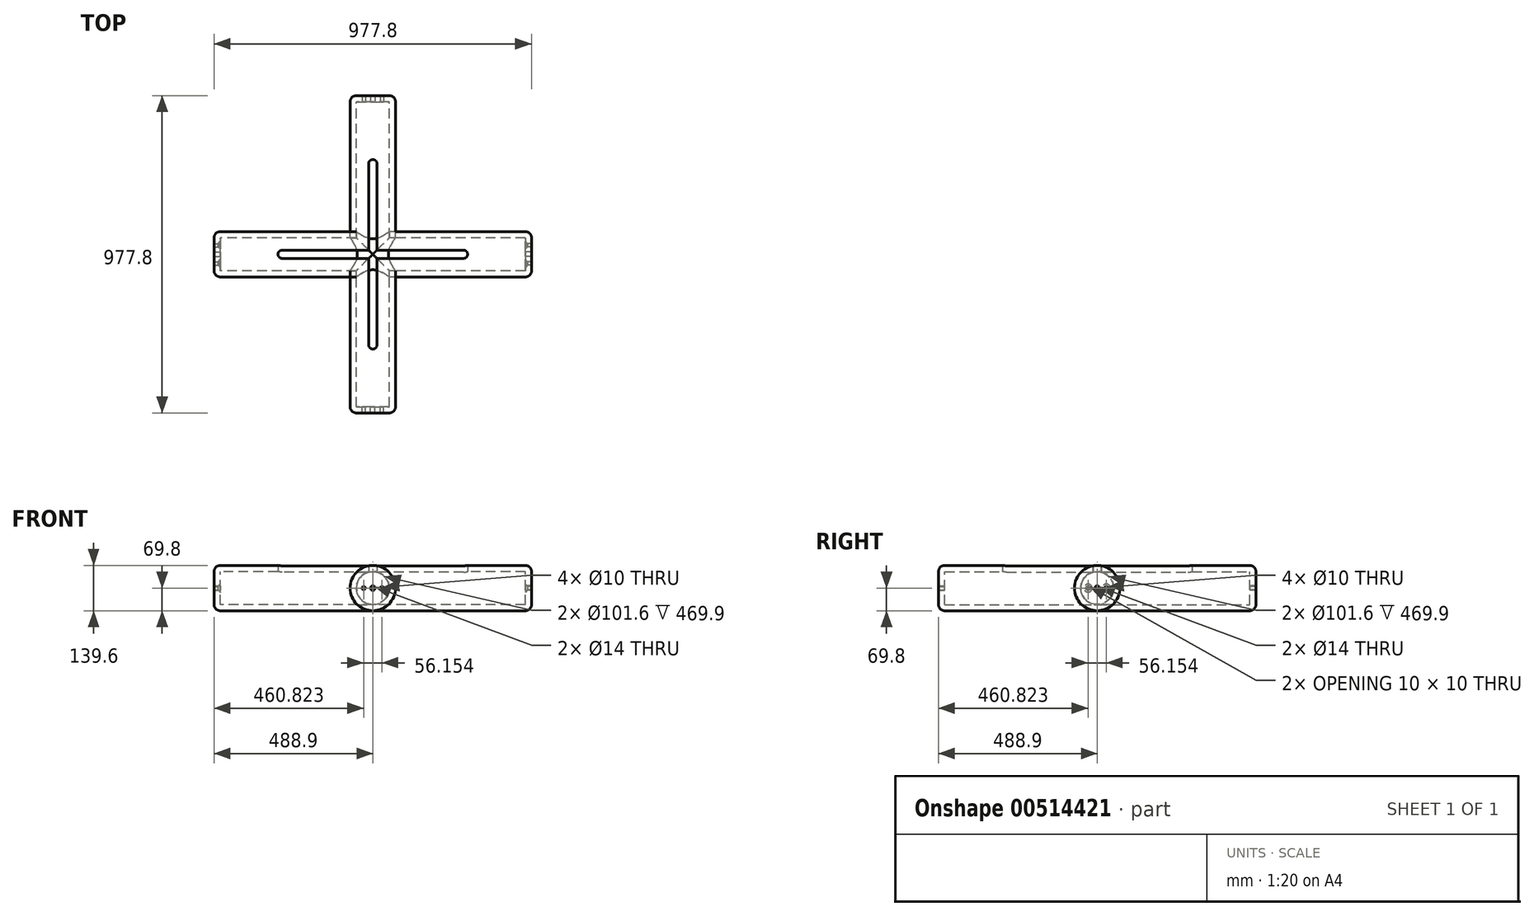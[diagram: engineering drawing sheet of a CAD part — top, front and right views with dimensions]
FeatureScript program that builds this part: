
annotation { "Feature Type Name" : "Feature", "Feature Type Description" : "" }
export const myFeature = defineFeature(function(context is Context, id is Id, definition is map)
    precondition{}
    {
        {
            var Q0;
            Q0=qCreatedBy(makeId("Front.planeOp"),FACE);
            var sketch = newSketch(context, id + "F0", { "sketchPlane" : qUnion([Q0])});
            skLineSegment(sketch, "E0", {"start": v(0, 19.05) * mm, "end": v(0, -19.05) * mm, "construction": true});
            skLineSegment(sketch, "E1", {"start": v(-19.05, 0) * mm, "end": v(19.05, 0) * mm, "construction": true});
            skPoint(sketch, "E2", {"position": v(0, 0) * mm});
            skCircle(sketch, "E3", {"center": v(0, 0) * mm, "radius": 50.8 * mm});
            skCircle(sketch, "E4.0", {"center": v(0, 0) * mm, "radius": 69.8 * mm});
            skSolve(sketch);
        }
        {
            var Q0;
            Q0=makeQuery(id+"F0.imprint","IMPRINT",FACE,{"disambiguationData":[TD([[makeQuery(id+"F0.imprint","IMPRINT",EDGE,{"derivedFrom":sQuery(id+"F0.wireOp",EDGE,"E3")}),-1.0]])]});
            extrude(context, id + "F1", {"entities" : qUnion([Q0]), "depth" : 939.8 * mm, "offsetDistance" : 25.4 * mm, "symmetric" : true});
        }
        {
            var Q0;
            Q0=qCreatedBy(makeId("Right.planeOp"),FACE);
            var sketch = newSketch(context, id + "F2", { "sketchPlane" : qUnion([Q0])});
            skPoint(sketch, "E5", {"position": v(0, 0) * mm});
            skCircle(sketch, "E6", {"center": v(0, 0) * mm, "radius": 50.8 * mm});
            skCircle(sketch, "E7.0", {"center": v(0, 0) * mm, "radius": 69.8 * mm});
            skSolve(sketch);
        }
        {
            var Q0;
            Q0=makeQuery(id+"F2.imprint","IMPRINT",FACE,{"disambiguationData":[TD([[makeQuery(id+"F2.imprint","IMPRINT",EDGE,{"derivedFrom":sQuery(id+"F2.wireOp",EDGE,"E6")}),-1.0]])]});
            extrude(context, id + "F3", {"entities" : qUnion([Q0]), "depth" : 939.8 * mm, "offsetDistance" : 25.4 * mm, "symmetric" : true});
        }
        {
            var Q0;
            Q0=sQuery(id+"F2.wireOp",VERTEX,"E5");
            var Q1;
            Q1=makeQuery(id+"F1.opExtrude","SWEPT_BODY",BODY,{"disambiguationData":[OSD([sQuery(id+"F0.wireOp",EDGE,"E3"),sQuery(id+"F0.wireOp",EDGE,"E4.0")])]});
            hole(context, id + "F4", {"style" : HoleStyle.SIMPLE, "endStyle" : HoleEndStyle.THROUGH, "oppositeDirection" : true, "holeDiameter" : 101.6 * mm, "isTappedThrough" : true, "tappedDepth" : 12.7 * mm, "tapClearance" : 3, "locations" : qUnion([Q0]), "scope" : qUnion([Q1]), "majorDiameter" : 6.35 * mm});
        }
        {
            var Q0;
            Q0=sQuery(id+"F2.wireOp",VERTEX,"E5");
            var Q1;
            Q1=makeQuery(id+"F1.opExtrude","SWEPT_BODY",BODY,{"disambiguationData":[OSD([sQuery(id+"F0.wireOp",EDGE,"E3"),sQuery(id+"F0.wireOp",EDGE,"E4.0")])]});
            hole(context, id + "F5", {"style" : HoleStyle.SIMPLE, "endStyle" : HoleEndStyle.THROUGH, "holeDiameter" : 101.6 * mm, "isTappedThrough" : true, "tappedDepth" : 12.7 * mm, "tapClearance" : 3, "locations" : qUnion([Q0]), "scope" : qUnion([Q1]), "majorDiameter" : 6.35 * mm});
        }
        {
            var Q0;
            Q0=sQuery(id+"F0.wireOp",VERTEX,"E2");
            var Q1;
            Q1=makeQuery(id+"F3.opExtrude","SWEPT_BODY",BODY,{"disambiguationData":[OSD([sQuery(id+"F2.wireOp",EDGE,"E6"),sQuery(id+"F2.wireOp",EDGE,"E7.0")])]});
            hole(context, id + "F6", {"style" : HoleStyle.SIMPLE, "endStyle" : HoleEndStyle.THROUGH, "oppositeDirection" : true, "holeDiameter" : 101.6 * mm, "isTappedThrough" : true, "tappedDepth" : 12.7 * mm, "tapClearance" : 3, "locations" : qUnion([Q0]), "scope" : qUnion([Q1]), "majorDiameter" : 6.35 * mm});
        }
        {
            var Q0;
            Q0=sQuery(id+"F0.wireOp",VERTEX,"E2");
            var Q1;
            Q1=makeQuery(id+"F3.opExtrude","SWEPT_BODY",BODY,{"disambiguationData":[OSD([sQuery(id+"F2.wireOp",EDGE,"E6"),sQuery(id+"F2.wireOp",EDGE,"E7.0")])]});
            hole(context, id + "F7", {"style" : HoleStyle.SIMPLE, "endStyle" : HoleEndStyle.THROUGH, "holeDiameter" : 101.6 * mm, "isTappedThrough" : true, "tappedDepth" : 12.7 * mm, "tapClearance" : 3, "locations" : qUnion([Q0]), "scope" : qUnion([Q1]), "majorDiameter" : 6.35 * mm});
        }
        {
            var Q0;
            Q0=qCreatedBy(makeId("Top.planeOp"),FACE);
            var sketch = newSketch(context, id + "F8", { "sketchPlane" : qUnion([Q0])});
            skLineSegment(sketch, "E8.bottom", {"start": v(-12.7, 419.1) * mm, "end": v(12.7, 419.1) * mm});
            skLineSegment(sketch, "E8.top", {"start": v(-12.7, -419.1) * mm, "end": v(12.7, -419.1) * mm});
            skLineSegment(sketch, "E8.left", {"start": v(-12.7, 419.1) * mm, "end": v(-12.7, -419.1) * mm});
            skLineSegment(sketch, "E8.right", {"start": v(12.7, 419.1) * mm, "end": v(12.7, -419.1) * mm});
            skLineSegment(sketch, "E9.bottom", {"start": v(-419.1, 12.7) * mm, "end": v(419.1, 12.7) * mm});
            skLineSegment(sketch, "E9.top", {"start": v(-419.1, -12.7) * mm, "end": v(419.1, -12.7) * mm});
            skLineSegment(sketch, "E9.left", {"start": v(-419.1, 12.7) * mm, "end": v(-419.1, -12.7) * mm});
            skLineSegment(sketch, "E9.right", {"start": v(419.1, 12.7) * mm, "end": v(419.1, -12.7) * mm});
            skArc(sketch, "E10", {"start": v(12.7, 279.4) * mm, "mid": v(0, 292.1) * mm, "end": v(-12.7, 279.4) * mm});
            skLineSegment(sketch, "E11", {"start": v(0, 279.4) * mm, "end": v(0, 0) * mm, "construction": true});
            skArc(sketch, "E12.1.0", {"start": v(-279.4, 12.7) * mm, "mid": v(-292.1, 0) * mm, "end": v(-279.4, -12.7) * mm});
            skArc(sketch, "E12.2.0", {"start": v(-12.7, -279.4) * mm, "mid": v(0, -292.1) * mm, "end": v(12.7, -279.4) * mm});
            skArc(sketch, "E12.3.0", {"start": v(279.4, -12.7) * mm, "mid": v(292.1, 0) * mm, "end": v(279.4, 12.7) * mm});
            skPoint(sketch, "E12.center", {"position": v(0, 0) * mm});
            skCircle(sketch, "E13", {"center": v(0, 0) * mm, "radius": 12.7 * mm, "construction": true});
            skSolve(sketch);
        }
        {
            var Q0;
            {var subQ5=sQuery(id+"F8.wireOp",EDGE,"E12.1.0");Q0=makeQuery(id+"F8.imprint","IMPRINT",FACE,{"disambiguationData":[TD([[makeQuery(id+"F8.imprint","IMPRINT",EDGE,{"derivedFrom":subQ5}),1.0]])]});}
            var Q1;
            {var subQ0=sQuery(id+"F8.wireOp",EDGE,"E10");Q1=makeQuery(id+"F8.imprint","IMPRINT",FACE,{"disambiguationData":[TD([[makeQuery(id+"F8.imprint","IMPRINT",EDGE,{"derivedFrom":subQ0}),1.0]])]});}
            var Q2;
            {var subQ5=sQuery(id+"F8.wireOp",EDGE,"E12.3.0");Q2=makeQuery(id+"F8.imprint","IMPRINT",FACE,{"disambiguationData":[TD([[makeQuery(id+"F8.imprint","IMPRINT",EDGE,{"derivedFrom":subQ5}),1.0]])]});}
            var Q3;
            {var subQ0=sQuery(id+"F8.wireOp",EDGE,"E12.2.0");Q3=makeQuery(id+"F8.imprint","IMPRINT",FACE,{"disambiguationData":[TD([[makeQuery(id+"F8.imprint","IMPRINT",EDGE,{"derivedFrom":subQ0}),1.0]])]});}
            var Q4;
            {var subQ0=sQuery(id+"F8.wireOp",EDGE,"E9.bottom");var subQ1=sQuery(id+"F8.wireOp",EDGE,"E8.left");var subQ2=makeQuery(id+"F8.imprint","INTERSECT",VERTEX,{"derivedFrom":[subQ1,subQ0]});Q4=makeQuery(id+"F8.imprint","IMPRINT",FACE,{"disambiguationData":[TD([[makeQuery(id+"F8.imprint","IMPRINT",EDGE,{"disambiguationData":[TD([[subQ2,-1.0]])],"derivedFrom":subQ1}),1.0]])]});}
            extrude(context, id + "F9", {"entities" : qUnion([Q0, Q1, Q2, Q3, Q4]), "operationType" : NewBodyOperationType.REMOVE, "depth" : 76.2 * mm, "offsetDistance" : 25.4 * mm});
        }
        {
            var Q0;
            Q0=makeQuery(id+"F3.opExtrude","CAP_FACE",FACE,{"disambiguationData":[OSD([sQuery(id+"F2.wireOp",EDGE,"E6"),sQuery(id+"F2.wireOp",EDGE,"E7.0")])],"isStart":true});
            var sketch = newSketch(context, id + "F10", { "sketchPlane" : qUnion([Q0])});
            skCircle(sketch, "E14", {"center": v(0, 0) * mm, "radius": 69.8 * mm});
            skCircle(sketch, "E15", {"center": v(-28.08, 0) * mm, "radius": 5 * mm});
            skCircle(sketch, "E16", {"center": v(28.08, 0) * mm, "radius": 5 * mm});
            skCircle(sketch, "E17", {"center": v(0, 0) * mm, "radius": 50.8 * mm, "construction": true});
            skCircle(sketch, "E18", {"center": v(0, 0) * mm, "radius": 7 * mm});
            skLineSegment(sketch, "E19", {"start": v(-7, 0) * mm, "end": v(7, 0) * mm, "construction": true});
            skLineSegment(sketch, "E20", {"start": v(0, 7) * mm, "end": v(0, -7) * mm, "construction": true});
            skSolve(sketch);
        }
        {
            var Q0;
            Q0=makeQuery(id+"F1.opExtrude","CAP_FACE",FACE,{"disambiguationData":[OSD([sQuery(id+"F0.wireOp",EDGE,"E3"),sQuery(id+"F0.wireOp",EDGE,"E4.0")])],"isStart":true});
            var sketch = newSketch(context, id + "F11", { "sketchPlane" : qUnion([Q0])});
            skCircle(sketch, "E21", {"center": v(0, 0) * mm, "radius": 69.8 * mm});
            skCircle(sketch, "E22", {"center": v(-28.08, 0) * mm, "radius": 5 * mm});
            skCircle(sketch, "E23", {"center": v(28.08, 0) * mm, "radius": 5 * mm});
            skCircle(sketch, "E24", {"center": v(0, 0) * mm, "radius": 50.8 * mm, "construction": true});
            skCircle(sketch, "E25", {"center": v(0, 0) * mm, "radius": 7 * mm});
            skLineSegment(sketch, "E26", {"start": v(0, 7) * mm, "end": v(0, -7) * mm, "construction": true});
            skLineSegment(sketch, "E27", {"start": v(7, 0) * mm, "end": v(-7, 0) * mm, "construction": true});
            skSolve(sketch);
        }
        {
            var Q0;
            Q0=makeQuery(id+"F3.opExtrude","CAP_FACE",FACE,{"disambiguationData":[OSD([sQuery(id+"F2.wireOp",EDGE,"E6"),sQuery(id+"F2.wireOp",EDGE,"E7.0")])],"isStart":false});
            var sketch = newSketch(context, id + "F12", { "sketchPlane" : qUnion([Q0])});
            skCircle(sketch, "E28", {"center": v(0, 0) * mm, "radius": 69.8 * mm});
            skCircle(sketch, "E29", {"center": v(-28.08, 0) * mm, "radius": 5 * mm});
            skCircle(sketch, "E30", {"center": v(28.08, 0) * mm, "radius": 5 * mm});
            skCircle(sketch, "E31", {"center": v(0, 0) * mm, "radius": 50.8 * mm, "construction": true});
            skCircle(sketch, "E32", {"center": v(0, 0) * mm, "radius": 7 * mm});
            skLineSegment(sketch, "E33", {"start": v(0, 7) * mm, "end": v(0, -7) * mm, "construction": true});
            skLineSegment(sketch, "E34", {"start": v(7, 0) * mm, "end": v(-7, 0) * mm, "construction": true});
            skSolve(sketch);
        }
        {
            var Q0;
            Q0=makeQuery(id+"F1.opExtrude","CAP_FACE",FACE,{"disambiguationData":[OSD([sQuery(id+"F0.wireOp",EDGE,"E3"),sQuery(id+"F0.wireOp",EDGE,"E4.0")])],"isStart":false});
            var sketch = newSketch(context, id + "F13", { "sketchPlane" : qUnion([Q0])});
            skCircle(sketch, "E35", {"center": v(0, 0) * mm, "radius": 69.8 * mm});
            skCircle(sketch, "E36", {"center": v(-28.08, 0) * mm, "radius": 5 * mm});
            skCircle(sketch, "E37", {"center": v(28.08, 0) * mm, "radius": 5 * mm});
            skCircle(sketch, "E38", {"center": v(0, 0) * mm, "radius": 50.8 * mm, "construction": true});
            skCircle(sketch, "E39", {"center": v(0, 0) * mm, "radius": 7 * mm});
            skLineSegment(sketch, "E40", {"start": v(0, 7) * mm, "end": v(0, -7) * mm, "construction": true});
            skLineSegment(sketch, "E41", {"start": v(-7, 0) * mm, "end": v(7, 0) * mm, "construction": true});
            skSolve(sketch);
        }
        {
            var Q0;
            Q0=makeQuery(id+"F11.imprint","IMPRINT",FACE,{"disambiguationData":[TD([[makeQuery(id+"F11.imprint","IMPRINT",EDGE,{"derivedFrom":sQuery(id+"F11.wireOp",EDGE,"E21")}),-1.0]])]});
            var Q1;
            Q1=makeQuery(id+"F11.imprint","IMPRINT",FACE,{"disambiguationData":[TD([[makeQuery(id+"F11.imprint","IMPRINT",EDGE,{"derivedFrom":sQuery(id+"F11.wireOp",EDGE,"E22")}),-1.0]])]});
            extrude(context, id + "F14", {"entities" : qUnion([Q0, Q1]), "operationType" : NewBodyOperationType.ADD, "depth" : 19 * mm, "offsetDistance" : 25.4 * mm});
        }
        {
            var Q0;
            Q0=makeQuery(id+"F10.imprint","IMPRINT",FACE,{"disambiguationData":[TD([[makeQuery(id+"F10.imprint","IMPRINT",EDGE,{"derivedFrom":sQuery(id+"F10.wireOp",EDGE,"E15")}),-1.0]])]});
            var Q1;
            Q1=makeQuery(id+"F10.imprint","IMPRINT",FACE,{"disambiguationData":[TD([[makeQuery(id+"F10.imprint","IMPRINT",EDGE,{"derivedFrom":sQuery(id+"F10.wireOp",EDGE,"E14")}),-1.0]])]});
            extrude(context, id + "F15", {"entities" : qUnion([Q0, Q1]), "operationType" : NewBodyOperationType.ADD, "depth" : 19 * mm, "offsetDistance" : 25.4 * mm});
        }
        {
            var Q0;
            Q0=makeQuery(id+"F12.imprint","IMPRINT",FACE,{"disambiguationData":[TD([[makeQuery(id+"F12.imprint","IMPRINT",EDGE,{"derivedFrom":sQuery(id+"F12.wireOp",EDGE,"E28")}),1.0]])]});
            var Q1;
            Q1=makeQuery(id+"F12.imprint","IMPRINT",FACE,{"disambiguationData":[TD([[makeQuery(id+"F12.imprint","IMPRINT",EDGE,{"derivedFrom":sQuery(id+"F12.wireOp",EDGE,"E29")}),-1.0]])]});
            extrude(context, id + "F16", {"entities" : qUnion([Q0, Q1]), "operationType" : NewBodyOperationType.ADD, "depth" : 19 * mm, "offsetDistance" : 25.4 * mm});
        }
        {
            var Q0;
            Q0=makeQuery(id+"F13.imprint","IMPRINT",FACE,{"disambiguationData":[TD([[makeQuery(id+"F13.imprint","IMPRINT",EDGE,{"derivedFrom":sQuery(id+"F13.wireOp",EDGE,"E36")}),-1.0]])]});
            var Q1;
            Q1=makeQuery(id+"F13.imprint","IMPRINT",FACE,{"disambiguationData":[TD([[makeQuery(id+"F13.imprint","IMPRINT",EDGE,{"derivedFrom":sQuery(id+"F13.wireOp",EDGE,"E35")}),1.0]])]});
            extrude(context, id + "F17", {"entities" : qUnion([Q0, Q1]), "operationType" : NewBodyOperationType.ADD, "depth" : 19 * mm, "offsetDistance" : 25.4 * mm});
        }
        {
            var Q0;
            Q0=makeQuery(id+"F15.opExtrude","CAP_EDGE",EDGE,{"disambiguationData":[OSD([sQuery(id+"F10.wireOp",EDGE,"E14")])],"isStart":false});
            var Q1;
            Q1=makeQuery(id+"F14.opExtrude","CAP_EDGE",EDGE,{"disambiguationData":[OSD([sQuery(id+"F11.wireOp",EDGE,"E21")])],"isStart":false});
            var Q2;
            Q2=makeQuery(id+"F16.opExtrude","CAP_EDGE",EDGE,{"disambiguationData":[OSD([sQuery(id+"F12.wireOp",EDGE,"E28")])],"isStart":false});
            var Q3;
            Q3=makeQuery(id+"F17.opExtrude","CAP_EDGE",EDGE,{"disambiguationData":[OSD([sQuery(id+"F13.wireOp",EDGE,"E35")])],"isStart":false});
            fillet(context, id + "F18", {"entities" : qUnion([Q0, Q1, Q2, Q3]), "radius" : 19 * mm, "tangentPropagation" : true, "allowEdgeOverflow" : false});
        }
        {
            var Q0;
            Q0=sQuery(id+"F12.wireOp",VERTEX,"E30.center");
            var Q1;
            Q1=sQuery(id+"F12.wireOp",VERTEX,"E29.center");
            var Q2;
            Q2=sQuery(id+"F13.wireOp",VERTEX,"E36.center");
            var Q3;
            Q3=sQuery(id+"F13.wireOp",VERTEX,"E37.center");
            var Q4;
            Q4=sQuery(id+"F10.wireOp",VERTEX,"E16.center");
            var Q5;
            Q5=sQuery(id+"F10.wireOp",VERTEX,"E15.center");
            var Q6;
            Q6=sQuery(id+"F11.wireOp",VERTEX,"E23.center");
            var Q7;
            Q7=sQuery(id+"F11.wireOp",VERTEX,"E22.center");
            var Q8;
            Q8=makeQuery(id+"F3.opExtrude","SWEPT_BODY",BODY,{"disambiguationData":[OSD([sQuery(id+"F2.wireOp",EDGE,"E6"),sQuery(id+"F2.wireOp",EDGE,"E7.0")])]});
            hole(context, id + "F19", {"style" : HoleStyle.C_SINK, "endStyle" : HoleEndStyle.BLIND, "oppositeDirection" : true, "holeDiameter" : 8 * mm, "cSinkDiameter" : 25 * mm, "cSinkAngle" : 100 * degree, "majorDiameter" : 6.35 * mm, "holeDepth" : 20 * mm, "isTappedThrough" : true, "tappedDepth" : 12.7 * mm, "tapClearance" : 3, "startFromSketch" : true, "locations" : qUnion([Q0, Q1, Q2, Q3, Q4, Q5, Q6, Q7]), "scope" : qUnion([Q8])});
        }
    });
